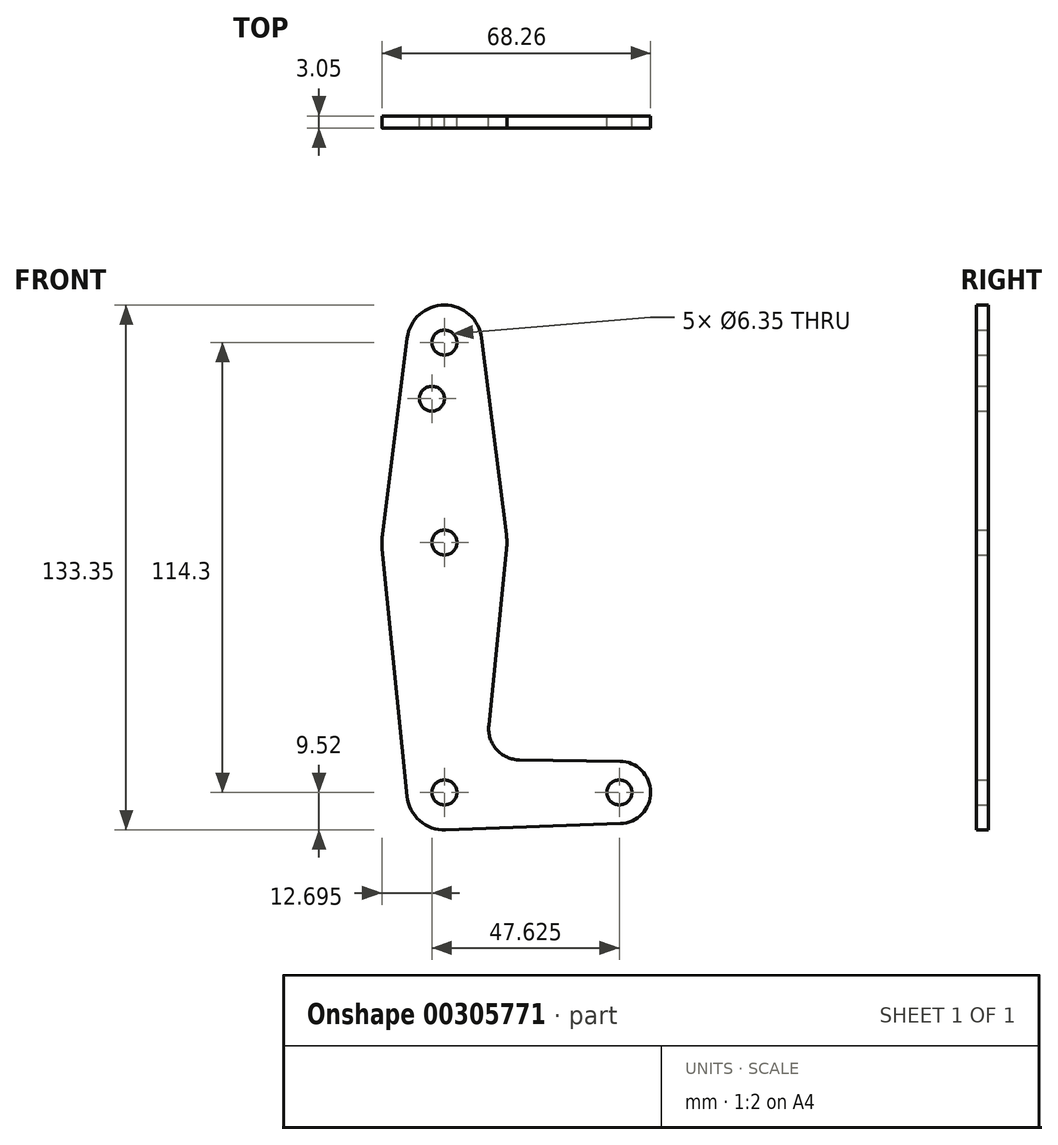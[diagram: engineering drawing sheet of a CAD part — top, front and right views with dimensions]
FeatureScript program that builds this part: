
annotation { "Feature Type Name" : "Feature", "Feature Type Description" : "" }
export const myFeature = defineFeature(function(context is Context, id is Id, definition is map)
    precondition{}
    {
        {
            var Q0;
            Q0=qCreatedBy(makeId("Front.planeOp"),FACE);
            var sketch = newSketch(context, id + "F0", { "sketchPlane" : qUnion([Q0])});
            skCircle(sketch, "E0", {"center": v(0, 0) * mm, "radius": 9.53 * mm});
            skCircle(sketch, "E1", {"center": v(0, 114.3) * mm, "radius": 9.53 * mm});
            skCircle(sketch, "E2", {"center": v(44.45, 0) * mm, "radius": 7.94 * mm});
            skLineSegment(sketch, "E3", {"start": v(0, 114.3) * mm, "end": v(0, 63.5) * mm, "construction": true});
            skLineSegment(sketch, "E4", {"start": v(0, 63.5) * mm, "end": v(0, 0) * mm, "construction": true});
            skLineSegment(sketch, "E5", {"start": v(0, 0) * mm, "end": v(44.45, 0) * mm, "construction": true});
            skLineSegment(sketch, "E6", {"start": v(9.45, 115.5) * mm, "end": v(15.75, 65.48) * mm});
            skLineSegment(sketch, "E7", {"start": v(-9.48, -0.95) * mm, "end": v(-15.8, 61.91) * mm});
            skCircle(sketch, "E8", {"center": v(0, 114.3) * mm, "radius": 3.18 * mm});
            skLineSegment(sketch, "E9", {"start": v(0.34, -9.52) * mm, "end": v(44.73, -7.93) * mm});
            skPoint(sketch, "E10.newPointA", {"position": v(9.57, 0) * mm});
            skCircle(sketch, "E11", {"center": v(0, 0) * mm, "radius": 3.18 * mm});
            skCircle(sketch, "E12", {"center": v(44.45, 0) * mm, "radius": 3.18 * mm});
            skCircle(sketch, "E13", {"center": v(-3.17, 100.03) * mm, "radius": 3.18 * mm});
            skCircle(sketch, "E14", {"center": v(0, 63.5) * mm, "radius": 15.88 * mm});
            skLineSegment(sketch, "E15", {"start": v(-9.45, 115.5) * mm, "end": v(-15.75, 65.48) * mm});
            skLineSegment(sketch, "E16", {"start": v(15.8, 61.91) * mm, "end": v(11.28, 17) * mm});
            skLineSegment(sketch, "E17", {"start": v(19.1, 8.26) * mm, "end": v(44.55, 7.94) * mm});
            skArc(sketch, "E18.filletArc", {"start": v(11.28, 17) * mm, "mid": v(13.26, 10.9) * mm, "end": v(19.1, 8.26) * mm});
            skCircle(sketch, "E19", {"center": v(0, 63.5) * mm, "radius": 3.18 * mm});
            skSolve(sketch);
        }
        {
            var Q0;
            Q0 = qSketchRegion(id + "F0", true);
            extrude(context, id + "F1", {"entities" : qUnion([Q0]), "depth" : 3.05 * mm});
        }
    });
